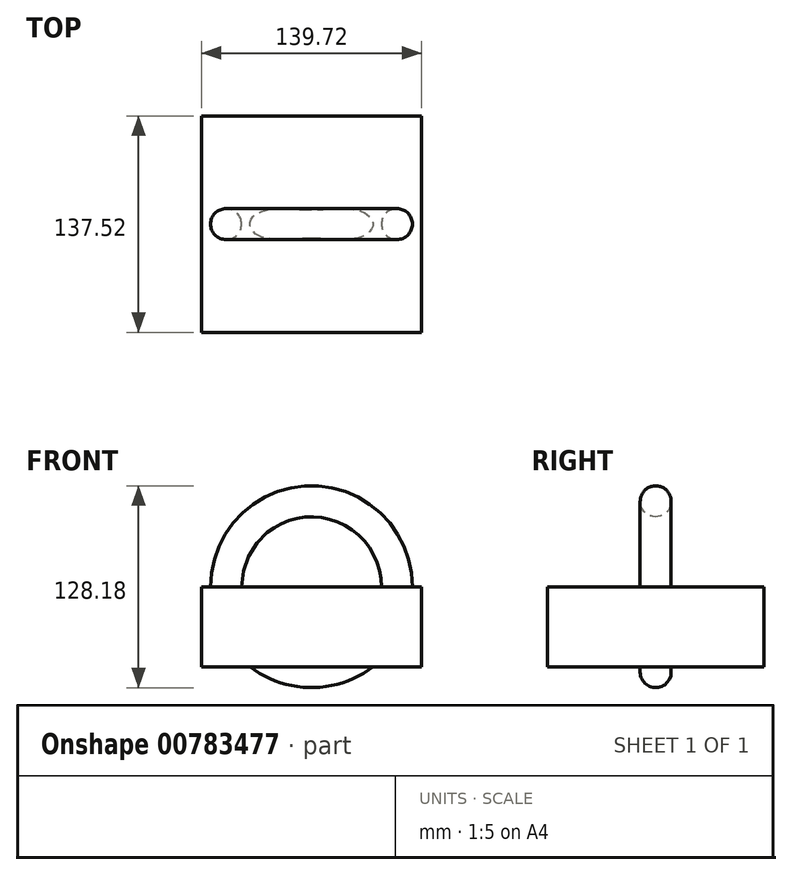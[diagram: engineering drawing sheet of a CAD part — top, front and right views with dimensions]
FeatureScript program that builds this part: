
annotation { "Feature Type Name" : "Feature", "Feature Type Description" : "" }
export const myFeature = defineFeature(function(context is Context, id is Id, definition is map)
    precondition{}
    {
        {
            var Q0;
            Q0=qCreatedBy(makeId("Top.planeOp"),FACE);
            var sketch = newSketch(context, id + "F0", { "sketchPlane" : qUnion([Q0])});
            skLineSegment(sketch, "E0.bottom", {"start": v(69.86, -68.76) * mm, "end": v(-69.86, -68.76) * mm});
            skLineSegment(sketch, "E0.top", {"start": v(69.86, 68.76) * mm, "end": v(-69.86, 68.76) * mm});
            skLineSegment(sketch, "E0.left", {"start": v(69.86, -68.76) * mm, "end": v(69.86, 68.76) * mm});
            skLineSegment(sketch, "E0.right", {"start": v(-69.86, -68.76) * mm, "end": v(-69.86, 68.76) * mm});
            skPoint(sketch, "E0.middle", {"position": v(0, 0) * mm});
            skLineSegment(sketch, "E1", {"start": v(0, 68.76) * mm, "end": v(0, -68.76) * mm});
            skSolve(sketch);
        }
        {
            var Q0;
            Q0=qCreatedBy(makeId("Top.planeOp"),FACE);
            var sketch = newSketch(context, id + "F1", { "sketchPlane" : qUnion([Q0])});
            skCircle(sketch, "E2", {"center": v(54.26, 0) * mm, "radius": 9.82 * mm});
            skSolve(sketch);
        }
        {
            var Q0;
            {var subQ0=sQuery(id+"F0.wireOp",EDGE,"E0.left");Q0=makeQuery(id+"F0.imprint","IMPRINT",FACE,{"disambiguationData":[TD([[makeQuery(id+"F0.imprint","IMPRINT",EDGE,{"derivedFrom":subQ0}),1.0]])]});}
            var Q1;
            {var subQ0=sQuery(id+"F0.wireOp",EDGE,"E0.right");Q1=makeQuery(id+"F0.imprint","IMPRINT",FACE,{"disambiguationData":[TD([[makeQuery(id+"F0.imprint","IMPRINT",EDGE,{"derivedFrom":subQ0}),-1.0]])]});}
            extrude(context, id + "F2", {"entities" : qUnion([Q0, Q1]), "depth" : -50.8 * mm, "offsetDistance" : 25.4 * mm});
        }
        {
            var Q0;
            Q0=makeQuery(id+"F1.imprint","IMPRINT",FACE,{"disambiguationData":[TD([[makeQuery(id+"F1.imprint","IMPRINT",EDGE,{"derivedFrom":sQuery(id+"F1.wireOp",EDGE,"E2")}),1.0]])]});
            var Q1;
            Q1=sQuery(id+"F0.wireOp",EDGE,"E1");
            revolve(context, id + "F3", {"operationType" : NewBodyOperationType.ADD, "surfaceOperationType" : NewSurfaceOperationType.NEW, "entities" : qUnion([Q0]), "axis" : qUnion([Q1]), "revolveType" : RevolveType.FULL});
        }
    });
